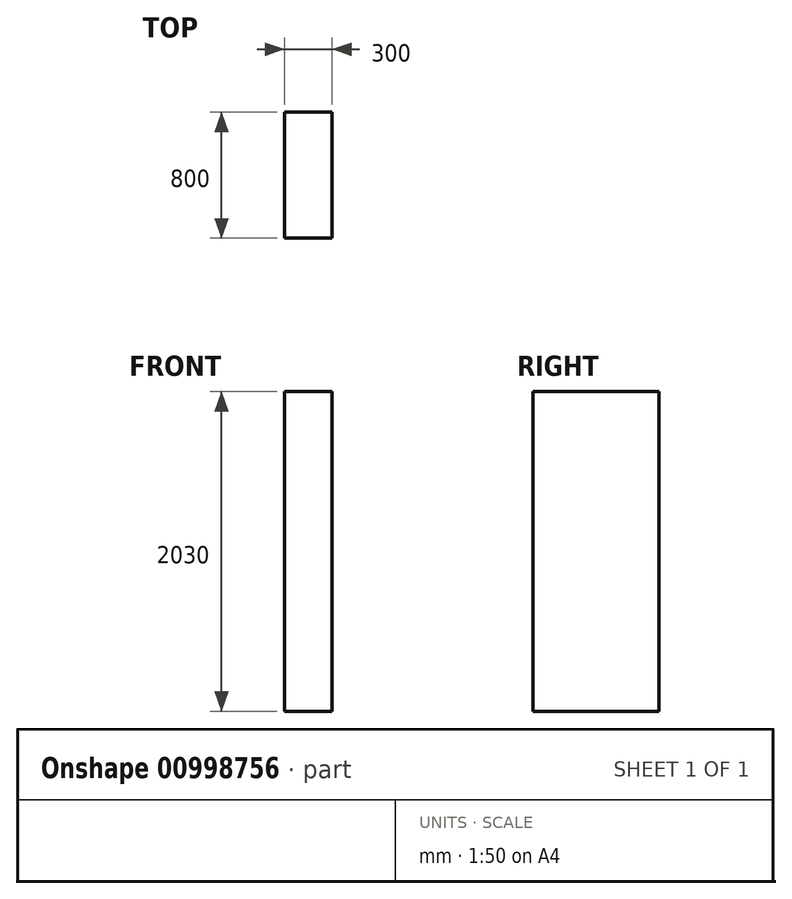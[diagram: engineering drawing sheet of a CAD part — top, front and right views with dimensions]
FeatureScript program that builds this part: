
annotation { "Feature Type Name" : "Feature", "Feature Type Description" : "" }
export const myFeature = defineFeature(function(context is Context, id is Id, definition is map)
    precondition{}
    {
        {
            var Q0;
            Q0=qCreatedBy(makeId("Top.planeOp"),FACE);
            var sketch = newSketch(context, id + "F0", { "sketchPlane" : qUnion([Q0])});
            skLineSegment(sketch, "E0.bottom", {"start": v(0, 0) * mm, "end": v(300, 0) * mm});
            skLineSegment(sketch, "E0.top", {"start": v(0, 800) * mm, "end": v(300, 800) * mm});
            skLineSegment(sketch, "E0.left", {"start": v(0, 0) * mm, "end": v(0, 800) * mm});
            skLineSegment(sketch, "E0.right", {"start": v(300, 0) * mm, "end": v(300, 800) * mm});
            skSolve(sketch);
        }
        {
            var Q0;
            Q0=makeQuery(id+"F0.imprint","IMPRINT",FACE,{"disambiguationData":[TD([[makeQuery(id+"F0.imprint","IMPRINT",EDGE,{"derivedFrom":sQuery(id+"F0.wireOp",EDGE,"E0.bottom")}),1.0]])]});
            extrude(context, id + "F1", {"entities" : qUnion([Q0]), "depth" : 2030 * mm, "offsetDistance" : 25 * mm});
        }
    });
